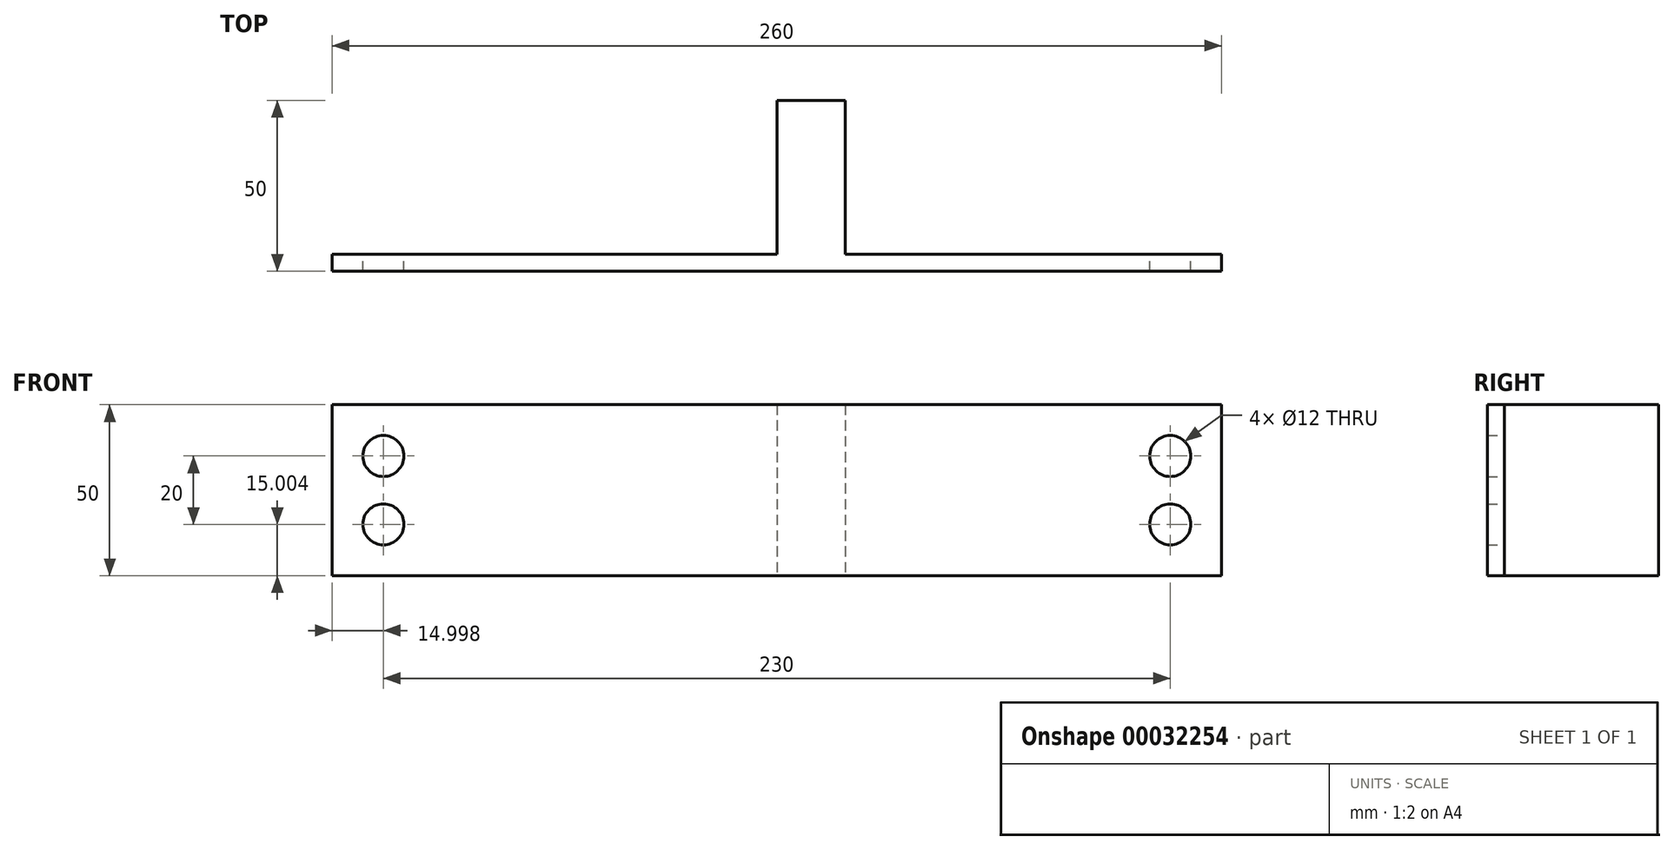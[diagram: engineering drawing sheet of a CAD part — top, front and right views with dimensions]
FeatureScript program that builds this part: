
annotation { "Feature Type Name" : "Feature", "Feature Type Description" : "" }
export const myFeature = defineFeature(function(context is Context, id is Id, definition is map)
    precondition{}
    {
        {
            var Q0;
            Q0=qCreatedBy(makeId("Front.planeOp"),FACE);
            var sketch = newSketch(context, id + "F0", { "sketchPlane" : qUnion([Q0])});
            skLineSegment(sketch, "E0.bottom", {"start": v(-122.62, -57.77) * mm, "end": v(137.38, -57.77) * mm});
            skLineSegment(sketch, "E0.top", {"start": v(-122.62, -7.77) * mm, "end": v(137.38, -7.77) * mm});
            skLineSegment(sketch, "E0.left", {"start": v(-122.62, -57.77) * mm, "end": v(-122.62, -7.77) * mm});
            skLineSegment(sketch, "E0.right", {"start": v(137.38, -57.77) * mm, "end": v(137.38, -7.77) * mm});
            skSolve(sketch);
        }
        {
            var Q0;
            Q0=makeQuery(id+"F0.imprint","IMPRINT",FACE,{"disambiguationData":[TD([[makeQuery(id+"F0.imprint","IMPRINT",EDGE,{"derivedFrom":sQuery(id+"F0.wireOp",EDGE,"E0.bottom")}),1.0]])]});
            extrude(context, id + "F1", {"entities" : qUnion([Q0]), "depth" : 5 * mm, "offsetDistance" : 25 * mm});
        }
        {
            var Q0;
            Q0=makeQuery(id+"F1.opExtrude","CAP_FACE",FACE,{"disambiguationData":[OSD([sQuery(id+"F0.wireOp",EDGE,"E0.bottom"),sQuery(id+"F0.wireOp",EDGE,"E0.top"),sQuery(id+"F0.wireOp",EDGE,"E0.left"),sQuery(id+"F0.wireOp",EDGE,"E0.right")])],"isStart":true});
            var sketch = newSketch(context, id + "F2", { "sketchPlane" : qUnion([Q0])});
            skLineSegment(sketch, "E1.bottom", {"start": v(-27.38, -7.77) * mm, "end": v(-7.38, -7.77) * mm});
            skLineSegment(sketch, "E1.top", {"start": v(-27.38, -57.77) * mm, "end": v(-7.38, -57.77) * mm});
            skLineSegment(sketch, "E1.left", {"start": v(-7.38, -7.77) * mm, "end": v(-7.38, -57.77) * mm});
            skLineSegment(sketch, "E1.right", {"start": v(-27.38, -7.77) * mm, "end": v(-27.38, -57.77) * mm});
            skLineSegment(sketch, "E2", {"start": v(-27.38, -32.77) * mm, "end": v(-7.38, -32.77) * mm, "construction": true});
            skLineSegment(sketch, "E3", {"start": v(-17.38, -32.77) * mm, "end": v(-17.38, -7.77) * mm, "construction": true});
            skSolve(sketch);
        }
        {
            var Q0;
            Q0 = qSketchRegion(id + "F2", true);
            extrude(context, id + "F3", {"entities" : qUnion([Q0]), "operationType" : NewBodyOperationType.ADD, "depth" : 45 * mm, "offsetDistance" : 25 * mm});
        }
        {
            var Q0;
            Q0=qCreatedBy(makeId("Front.planeOp"),FACE);
            var sketch = newSketch(context, id + "F4", { "sketchPlane" : qUnion([Q0])});
            skLineSegment(sketch, "E4.0", {"start": v(137.38, -57.77) * mm, "end": v(137.38, -7.77) * mm});
            skLineSegment(sketch, "E5.0", {"start": v(-122.62, -57.77) * mm, "end": v(-122.62, -7.77) * mm});
            skLineSegment(sketch, "E6", {"start": v(137.38, -22.77) * mm, "end": v(-122.62, -22.77) * mm, "construction": true});
            skLineSegment(sketch, "E7", {"start": v(137.38, -42.77) * mm, "end": v(-122.62, -42.77) * mm, "construction": true});
            skCircle(sketch, "E8", {"center": v(122.38, -42.77) * mm, "radius": 6 * mm});
            skLineSegment(sketch, "E9", {"start": v(122.38, -42.77) * mm, "end": v(122.38, -22.77) * mm, "construction": true});
            skCircle(sketch, "E10", {"center": v(122.38, -22.77) * mm, "radius": 6 * mm});
            skLineSegment(sketch, "E11", {"start": v(7.38, 50.35) * mm, "end": v(7.38, -74.21) * mm, "construction": true});
            skCircle(sketch, "E12.MirrorC", {"center": v(-107.62, -42.77) * mm, "radius": 6 * mm});
            skCircle(sketch, "E13.MirrorC", {"center": v(-107.62, -22.77) * mm, "radius": 6 * mm});
            skSolve(sketch);
        }
        {
            var Q0;
            Q0 = qSketchRegion(id + "F4", true);
            extrude(context, id + "F5", {"entities" : qUnion([Q0]), "operationType" : NewBodyOperationType.REMOVE, "endBound" : BoundingType.UP_TO_NEXT, "depth" : 25 * mm, "offsetDistance" : 25 * mm});
        }
    });
